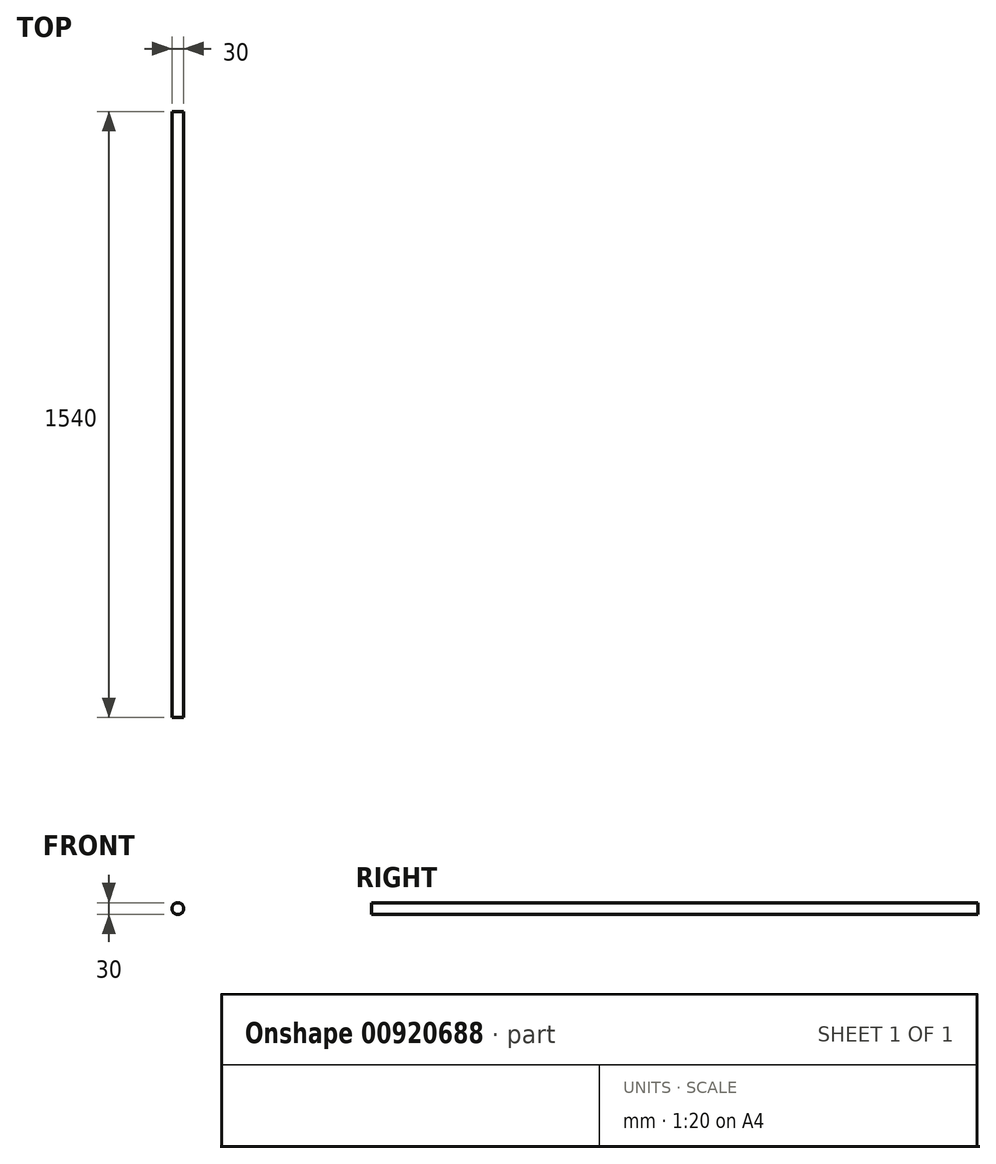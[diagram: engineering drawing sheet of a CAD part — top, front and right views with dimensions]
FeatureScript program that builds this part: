
annotation { "Feature Type Name" : "Feature", "Feature Type Description" : "" }
export const myFeature = defineFeature(function(context is Context, id is Id, definition is map)
    precondition{}
    {
        {
            var Q0;
            Q0=qCreatedBy(makeId("Front.planeOp"),FACE);
            var sketch = newSketch(context, id + "F0", { "sketchPlane" : qUnion([Q0])});
            skCircle(sketch, "E0", {"center": v(0, 0) * mm, "radius": 15 * mm});
            skSolve(sketch);
        }
        {
            var Q0;
            Q0=makeQuery(id+"F0.imprint","IMPRINT",FACE,{"disambiguationData":[TD([[makeQuery(id+"F0.imprint","IMPRINT",EDGE,{"derivedFrom":sQuery(id+"F0.wireOp",EDGE,"E0")}),1.0]])]});
            extrude(context, id + "F1", {"entities" : qUnion([Q0]), "endBound" : BoundingType.SYMMETRIC, "depth" : 1540 * mm, "offsetDistance" : 25 * mm});
        }
    });
